# Revit family: FY-B-TY3451_Imperial
name_source: partatom
category: Sprinklers
units: mm (PartAtom-declared; Revit-internal decimal feet)

## family parameters
Always vertical = Yes
Cut with Voids When Loaded = No
Maintain Annotation Orientation = No
OmniClass Number = 23.65.70.17.11.24
OmniClass Title = Fire Fighting Sprinkler Heads
Part Type = Normal
Room Calculation Point = No
Round Connector Dimension = Use Diameter
Shared = No
Work Plane-Based = No

## types (42) — shared parameters
COBie = Yes
COBie.Component.Name = Sprinklers:Vertical SW_SIN
COBie.Type = Yes
COBie.Type.AssetType = Fixed
COBie.Type.Category = Pr_70_55_97_84:Sprinklers
COBie.Type.Manufacturer = Tyco Fire Protection Products
COBie.Type.Material = Bronze
COBie.Type.NominalHeight = 0' - 0"
COBie.Type.NominalLength = 0' - 0"
COBie.Type.NominalWidth = 0' - 0"
COBie.Type.Shape = Cylinder
COBie.Type.WarrantyGuarantorParts = http://tycofsbp.com
TFPPTerms_of_Sale.pdf
Coverage = Standard
Coverage_ = Standard
Default Elevation = 0' - 0"
K-Factor = 5.5493
Manufacturer = Tyco Fire Protection Products
Manufacturer URL = www.tyco-fire.com
Material_ = Bronze
Model = TY-B
Nominal Diameter 1 = 1"
Orifice = Standard
Orifice Size = 0"
Outside Diameter 1 = 1"
Response = Standard
Response_ = Standard
SIN No = TY3451
Takeout 1 = 2"
Technical Data Sheet No = TFP161
zero-valued in all types: COBie.Type.ReplacementCost, Style Id

## per-type parameters (varying)
| type | COBie.Component.Description | COBie.Type.Colour | COBie.Type.DurationUnit | COBie.Type.Finish | COBie.Type.ModelNumber | COBie.Type.ModelReference | COBie.Type.Size | COBie.Type.WarrantyDescription | Description | Finish_ | Part No | Temperature Rating |
| Vertical Sidewall Brass 135°F/57°C 5.6K ½" NPT_57-575-1-135 | TY-B Wet Vertical SW  57.2°C K80 DN15 NPT Br | Yellow | year | Natural Brass | 57-575-1-135 | TY-B Wet Vertical SW  57.2°C K80 DN15 NPT Br | 1/2"(DN15) |  | TY-B Vertical Sidewall Brass 135°F/57°C 5.6K ½" NPT_57-575-1-135 | Natural Brass | 57-575-1-135 | 135 °F |
| Vertical Sidewall Brass 155°F/68°C 5.6K ½" NPT_57-575-1-155 | TY-B Wet Vertical SW  68.3°C K80 DN15 NPT Br | Yellow | year | Natural Brass | 57-575-1-155 | TY-B Wet Vertical SW  68.3°C K80 DN15 NPT Br | 1/2"(DN15) |  | TY-B Vertical Sidewall Brass 155°F/68°C 5.6K ½" NPT_57-575-1-155 | Natural Brass | 57-575-1-155 | 155 °F |
| Vertical Sidewall Brass 175°F/79°C 5.6K ½" NPT_57-575-1-175 | TY-B Wet Vertical SW  79.4°C K80 DN15 NPT Br | Yellow | year | natural Brass | 57-575-1-175 | TY-B Wet Vertical SW  79.4°C K80 DN15 NPT Br | 1/2"(DN15) |  | TY-B Vertical Sidewall Brass 175°F/79°C 5.6K ½" NPT_57-575-1-175 | Natural Brass | 57-575-1-175 | 175 °F |
| Vertical Sidewall Brass 200°F/93°C 5.6K ½" NPT_57-575-1-200 | TY-B Wet Vertical SW  93.3°C K80 DN15 NPT Br | Yellow | year | Natural Brass | 57-575-1-200 | TY-B Wet Vertical SW  93.3°C K80 DN15 NPT Br | 1/2"(DN15) |  | TY-B Vertical Sidewall Brass 200°F/93°C 5.6K ½" NPT_57-575-1-200 | Natural Brass | 57-575-1-200 | 200 °F |
| Vertical Sidewall Brass 286°F/141°C 5.6K ½" NPT_57-575-1-286 | TY-B Wet Vertical SW  141.1°C K80 DN15 NPT Br | Yellow | year | Natural Brass | 57-575-1-286 | TY-B Wet Vertical SW  141.1°C K80 DN15 NPT Br | 1/2"(DN15) |  | TY-B Vertical Sidewall Brass 286°F/141°C 5.6K ½" NPT_57-575-1-286 | Natural Brass | 57-575-1-286 | 286 °F |
| Vertical Sidewall Brass 360°F/182°C 5.6K ½" NPT_57-575-1-360 | TY-B Wet Vertical SW  182.2°C K80 DN15 NPT Br | Yellow | year | Natural Brass | 57-575-1-360 | TY-B Wet Vertical SW  182.2°C K80 DN15 NPT Br | 1/2"(DN15) |  | TY-B Vertical Sidewall Brass 360°F/182°C 5.6K ½" NPT_57-575-1-360 | Natural Brass | 57-575-1-360 | 360 °F |
| Vertical Sidewall White RAL9010 135°F/57°C 5.6K ½" NPT_57-575-3-135 | TY-B Wet Vertical SW  57.2°C K80 DN15 NPT Wh9010 | White | year | Pure White | 57-575-3-135 | TY-B Wet Vertical SW  57.2°C K80 DN15 NPT Wh9010 | 1/2"(DN15) |  | TY-B Vertical Sidewall White RAL9010 135°F/57°C 5.6K ½" NPT_57-575-3-135 | White RAL9010 | 57-575-3-135 | 135 °F |
| Vertical Sidewall White RAL9010 155°F/68°C 5.6K ½" NPT_57-575-3-155 | TY-B Wet Vertical SW  68.3°C K80 DN15 NPT Wh9010 | White |  | Pure White | 57-575-3-155 | TY-B Wet Vertical SW  68.3°C K80 DN15 NPT Wh9010 | 1/2"(DN15) |  | TY-B Vertical Sidewall White RAL9010 155°F/68°C 5.6K ½" NPT_57-575-3-155 | White RAL9010 | 57-575-3-155 | 155 °F |
| Vertical Sidewall White RAL9010 175°F/79°C 5.6K ½" NPT_57-575-3-175 | TY-B Wet Vertical SW  79.4°C K80 DN15 NPT Wh9010 | White | year | Pure White | 57-575-3-175 | TY-B Wet Vertical SW  79.4°C K80 DN15 NPT Wh9010 | 1/2"'(DN15) |  | TY-B Vertical Sidewall White RAL9010 175°F/79°C 5.6K ½" NPT_57-575-3-175 | White RAL9010 | 57-575-3-175 | 175 °F |
| Vertical Sidewall White RAL9010 200°F/93°C 5.6K ½" NPT_57-575-3-200 | TY-B Wet Vertical SW  93.3°C K80 DN15 NPT Wh9010 | White | year | Pure White | 57-575-3-200 | TY-B Wet Vertical SW  93.3°C K80 DN15 NPT Wh9010 | 1/2"(DN15) |  | TY-B Vertical Sidewall White RAL9010 200°F/93°C 5.6K ½" NPT_57-575-3-200 | White RAL9010 | 57-575-3-200 | 200 °F |
| Vertical Sidewall White RAL9010 286°F/141°C 5.6K ½" NPT_57-575-3-286 | TY-B Wet Vertical SW  141.1°C K80 DN15 NPT Wh9010 | White | year | Pure White | 57-575-3-286 | TY-B Wet Vertical SW  141.1°C K80 DN15 NPT Wh9010 | 1/2"(DN15) |  | TY-B Vertical Sidewall White RAL9010 286°F/141°C 5.6K ½" NPT_57-575-3-286 | White RAL9010 | 57-575-3-286 | 286 °F |
| Vertical Sidewall White RAL9010 360°F/182°C 5.6K ½" NPT_57-575-3-360 | TY-B Wet Vertical SW  182.2°C K80 DN15 NPT Wh9010 | White | year | Pure White | 57-575-3-360 | TY-B Wet Vertical SW  182.2°C K80 DN15 NPT Wh9010 | 1/2"(DN15) |  | TY-B Vertical Sidewall White RAL9010 360°F/182°C 5.6K ½" NPT_57-575-3-360 | White RAL9010 | 57-575-3-360 | 360 °F |
| Vertical Sidewall White 135°F/57°C 5.6K ½" NPT_57-575-4-135 | TY-B Wet Vertical SW  57.2°C K80 DN15 NPT Wh9003 | White | year | Signal White | 57-575-4-135 | TY-B Wet Vertical SW  57.2°C K80 DN15 NPT Wh9003 | 1/2"(DN15) |  | TY-B Vertical Sidewall White 135°F/57°C 5.6K ½" NPT_57-575-4-135 | White RAL9003 | 57-575-4-135 | 135 °F |
| Vertical Sidewall White 155°F/68°C 5.6K ½" NPT_57-575-4-155 | TY-B Wet Vertical SW  68.3°C K80 DN15 NPT Wh9003 | White | year | Signal White | 57-575-4-155 | TY-B Wet Vertical SW  68.3°C K80 DN15 NPT Wh9003 | 1/2"(DN15) |  | TY-B Vertical Sidewall White 155°F/68°C 5.6K ½" NPT_57-575-4-155 | White RAL9003 | 57-575-4-155 | 155 °F |
| Vertical Sidewall White 175°F/79°C 5.6K ½" NPT_57-575-4-175 | TY-B Wet Vertical SW  79.4°C K80 DN15 NPT Wh9003 | White | year | Signal White | 57-575-4-175 | TY-B Wet Vertical SW  79.4°C K80 DN15 NPT Wh9003 | 1/2"(DN15) |  | TY-B Vertical Sidewall White 175°F/79°C 5.6K ½" NPT_57-575-4-175 | White RAL9003 | 57-575-4-175 | 175 °F |
| Vertical Sidewall White 200°F/93°C 5.6K ½" NPT_57-575-4-200 | TY-B Wet Vertical SW  93.3°C K80 DN15 NPT Wh9003 | White | year | Signal White | 57-575-4-200 | TY-B Wet Vertical SW  93.3°C K80 DN15 NPT Wh9003 | 1/2"(DN15) |  | TY-B Vertical Sidewall White 200°F/93°C 5.6K ½" NPT_57-575-4-200 | White RAL9003 | 57-575-4-200 | 200 °F |
| Vertical Sidewall White 286°F/141°C 5.6K ½" NPT_57-575-4-286 | TY-B Wet Vertical SW  141.1°C K80 DN15 NPT Wh9003 | White | year | Signal White | 57-575-4-286 | TY-B Wet Vertical SW  141.1°C K80 DN15 NPT Wh9003 | 1/2"(DN15) | On-site Sprinkler Replacement Warranty | TY-B Vertical Sidewall White 286°F/141°C 5.6K ½" NPT_57-575-4-286 | White RAL9003 | 57-575-4-286 | 286 °F |
| Vertical Sidewall White 360°F/182°C 5.6K ½" NPT_57-575-4-360 | TY-B Wet Vertical SW  182.2°C K80 DN15 NPT Wh9003 | White | year | Signal White | 57-575-4-360 | TY-B Wet Vertical SW  182.2°C K80 DN15 NPT Wh9003 | 1/2"(DN15) |  | TY-B Vertical Sidewall White 360°F/182°C 5.6K ½" NPT_57-575-4-360 | White RAL9003 | 57-575-4-360 | 360 °F |
| Vertical Sidewall JetBlack 155°F/68°C 5.6K ½" NPT_57-575-5-155 | TY-B Wet Vertical SW  68.3°C K80 DN15 NPT JBlk | Black | year | Jet Black | 57-575-5-155 | TY-B Wet Vertical SW  68.3°C K80 DN15 NPT JBlk | 1/2"(DN15) |  | TY-B Vertical Sidewall JetBlack 155°F/68°C 5.6K ½" NPT_57-575-5-155 | Jet Black RAL9005 | 57-575-5-155 | 155 °F |
| Vertical Sidewall JetBlack 200°F/93°C 5.6K ½" NPT_57-575-5-200 | TY-B Wet Vertical SW  93.3°C K80 DN15 NPT JBlk | Black | year | Jet Black | 57-575-5-200 | TY-B Wet Vertical SW  93.3°C K80 DN15 NPT JBlk | 1/2"(DN15) |  | TY-B Vertical Sidewall JetBlack 200°F/93°C 5.6K ½" NPT_57-575-5-200 | Jet Black RAL9005 | 57-575-5-200 | 200 °F |
| Vertical Sidewall Wax 135°F/57°C 5.6K ½" NPT_57-575-6-135 | TY-B Wet Vertical SW  57.2°C K80 DN15 NPT Wx | Gray | year | Wax Coated | 57-575-6-135 | TY-B Wet Vertical SW  57.2°C K80 DN15 NPT Wx | 1/2"(DN15) |  | TY-B Vertical Sidewall Wax 135°F/57°C 5.6K ½" NPT_57-575-6-135 | Wax Coated | 57-575-6-135 | 135 °F |
| Vertical Sidewall Wax 155°F/68°C 5.6K ½" NPT_57-575-6-155 | TY-B Wet Vertical SW  68.3°C K80 DN15 NPT Wx | Gray | year | Wax Coated | 57-575-6-155 | TY-B Wet Vertical SW  68.3°C K80 DN15 NPT Wx | 1/2"(DN15) |  | TY-B Vertical Sidewall Wax 155°F/68°C 5.6K ½" NPT_57-575-6-155 | Wax Coated | 57-575-6-155 | 155 °F |
| Vertical Sidewall Wax 175°F/79°C 5.6K ½" NPT_57-575-6-175 | TY-B Wet Vertical SW  79.4°C K80 DN15 NPT Wx | Gray | year | Wax Coated | 57-575-6-175 | TY-B Wet Vertical SW  79.4°C K80 DN15 NPT Wx | 1/2"(DN15) |  | TY-B Vertical Sidewall Wax 175°F/79°C 5.6K ½" NPT_57-575-6-175 | Wax Coated | 57-575-6-175 | 175 °F |
| Vertical Sidewall Wax 200°F/93°C 5.6K ½" NPT_57-575-6-200 | TY-B Wet Vertical SW  93.3°C K80 DN15 NPT Wx | Gray | year | Wax Coated | 57-575-6-200 | TY-B Wet Vertical SW  93.3°C K80 DN15 NPT Wx | 1/2"(DN15) |  | TY-B Vertical Sidewall Wax 200°F/93°C 5.6K ½" NPT_57-575-6-200 | Wax Coated | 57-575-6-200 | 200 °F |
| Vertical Sidewall Wax 286°F/141°C 5.6K ½" NPT_57-575-6-286 | TY-B Wet Vertical SW  141.1°C K80 DN15 NPT Wx | Gray | year | Wax Coated | 57-575-6-286 | TY-B Wet Vertical SW  141.1°C K80 DN15 NPT Wx | 1/2"(DN15) |  | TY-B Vertical Sidewall Wax 286°F/141°C 5.6K ½" NPT_57-575-6-286 | Wax Coated | 57-575-6-286 | 286 °F |
| Vertical Sidewall Lead 135°F/57°C 5.6K ½" NPT_57-575-7-135 | TY-B Wet Vertical SW  57.2°C K80 DN15 NPT Lead | Gray | year | Lead Coated | 57-575-7-135 | TY-B Wet Vertical SW  57.2°C K80 DN15 NPT Lead | 1/2"(DN15) |  | TY-B Vertical Sidewall Lead 135°F/57°C 5.6K ½" NPT_57-575-7-135 | Lead Coated | 57-575-7-135 | 135 °F |
| Vertical Sidewall Lead 155°F/68°C 5.6K ½" NPT_57-575-7-155 | TY-B Wet Vertical SW  68.3°C K80 DN15 NPT Lead | Gray | year | Lead Coated | 57-575-7-155 | TY-B Wet Vertical SW  68.3°C K80 DN15 NPT Lead | 1/2"(DN15) |  | TY-B Vertical Sidewall Lead 155°F/68°C 5.6K ½" NPT_57-575-7-155 | Lead Coated | 57-575-7-155 | 155 °F |
| Vertical Sidewall Lead 175°F/79°C 5.6K ½" NPT_57-575-7-175 | TY-B Wet Vertical SW  79.4°C K80 DN15 NPT Lead | Gray | year | Lead Coated | 57-575-7-175 | TY-B Wet Vertical SW  79.4°C K80 DN15 NPT Lead | 1/2"(DN15) |  | TY-B Vertical Sidewall Lead 175°F/79°C 5.6K ½" NPT_57-575-7-175 | Lead Coated | 57-575-7-175 | 175 °F |
| Vertical Sidewall Lead 200°F/93°C 5.6K ½" NPT_57-575-7-200 | TY-B Wet Vertical SW  93.3°C K80 DN15 NPT Lead | Gray | year | Lead Coated | 57-575-7-200 | TY-B Wet Vertical SW  93.3°C K80 DN15 NPT Lead | 1/2"(DN15) |  | TY-B Vertical Sidewall Lead 200°F/93°C 5.6K ½" NPT_57-575-7-200 | Lead Coated | 57-575-7-200 | 200 °F |
| Vertical Sidewall Lead 286°F/141°C 5.6K ½" NPT_57-575-7-286 | TY-B Wet Vertical SW  141.1°C K80 DN15 NPT Lead | Gray | year | Lead Coated | 57-575-7-286 | TY-B Wet Vertical SW  141.1°C K80 DN15 NPT Lead | 1/2"(DN15) |  | TY-B Vertical Sidewall Lead 286°F/141°C 5.6K ½" NPT_57-575-7-286 | Lead Coated | 57-575-7-286 | 286 °F |
| Vertical Sidewall Lead 360°F/182°C 5.6K ½" NPT_57-575-7-360 | TY-B Wet Vertical SW  182.2°C K80 DN15 NPT Lead | Gray | year | Lead Coated | 57-575-7-360 | TY-B Wet Vertical SW  182.2°C K80 DN15 NPT Lead | 1/2"(DN15) |  | TY-B Vertical Sidewall Lead 360°F/182°C 5.6K ½" NPT_57-575-7-360 | Lead Coated | 57-575-7-360 | 360 °F |
| Vertical Sidewall Wax Over Lead 135°F/57°C 5.6K ½" NPT_57-575-8-135 | TY-B Wet Vertical SW  57.2°C K80 DN15 NPT WoL | Gray | year | Wax Over Lead | 57-575-8-135 | TY-B Wet Vertical SW  57.2°C K80 DN15 NPT WoL | 1/2"(DN15) |  | TY-B Vertical Sidewall Wax Over Lead 135°F/57°C 5.6K ½" NPT_57-575-8-135 | Wax Over Lead | 57-575-8-135 | 135 °F |
| Vertical Sidewall Wax Over Lead 155°F/68°C 5.6K ½" NPT_57-575-8-155 | TY-B Wet Vertical SW  68.3°C K80 DN15 NPT WoL | Gray | year | Wax Over Lead | 57-575-8-155 | TY-B Wet Vertical SW  68.3°C K80 DN15 NPT WoL | 1/2"(DN15) |  | TY-B Vertical Sidewall Wax Over Lead 155°F/68°C 5.6K ½" NPT_57-575-8-155 | Wax Over Lead | 57-575-8-155 | 155 °F |
| Vertical Sidewall Wax Over Lead 175°F/79°C 5.6K ½" NPT_57-575-8-175 | TY-B Wet Vertical SW  79.4°C K80 DN15 NPT WoL | Gray | year | Wax Over Lead | 57-575-8-175 | TY-B Wet Vertical SW  79.4°C K80 DN15 NPT WoL | 1/2"(DN15) |  | TY-B Vertical Sidewall Wax Over Lead 175°F/79°C 5.6K ½" NPT_57-575-8-175 | Wax Over Lead | 57-575-8-175 | 175 °F |
| Vertical Sidewall Wax Over Lead 200°F/93°C 5.6K ½" NPT_57-575-8-200 | TY-B Wet Vertical SW  93.3°C K80 DN15 NPT WoL | Gray | year | Wax Over Lead | 57-575-8-200 | TY-B Wet Vertical SW  93.3°C K80 DN15 NPT WoL | 1/2"(DN15) |  | TY-B Vertical Sidewall Wax Over Lead 200°F/93°C 5.6K ½" NPT_57-575-8-200 | Wax Over Lead | 57-575-8-200 | 200 °F |
| Vertical Sidewall Wax Over Lead 286°F/141°C 5.6K ½" NPT_57-575-8-286 | TY-B Wet Vertical SW  141.1°C K80 DN15 NPT WoL | Gray | year | Wax Over lead | 57-575-8-286 | TY-B Wet Vertical SW  141.1°C K80 DN15 NPT WoL | 1/2"(DN15) |  | TY-B Vertical Sidewall Wax Over Lead 286°F/141°C 5.6K ½" NPT_57-575-8-286 | Wax Over Lead | 57-575-8-286 | 286 °F |
| Vertical Sidewall Chrome 135°F/57°C 5.6K ½" NPT_57-575-9-135 | TY-B Wet Vertical SW  57.2°C K80 DN15 NPT Chr | Silver | year | Chrome Plated | 57-575-9-135 | TY-B Wet Vertical SW  57.2°C K80 DN15 NPT Chr | 1/2"(DN15) |  | TY-B Vertical Sidewall Chrome 135°F/57°C 5.6K ½" NPT_57-575-9-135 | Chrome Plated | 57-575-9-135 | 135 °F |
| Vertical Sidewall Chrome 155°F/68°C 5.6K ½" NPT_57-575-9-155 | TY-B Wet Vertical SW  68.3°C K80 DN15 NPT Chr | Silver | year | Chrome Plated | 57-575-9-155 | TY-B Wet Vertical SW  68.3°C K80 DN15 NPT Chr | 1/2"(DN15) |  | TY-B Vertical Sidewall Chrome 155°F/68°C 5.6K ½" NPT_57-575-9-155 | Chrome Plated | 57-575-9-155 | 155 °F |
| Vertical Sidewall Chrome 175°F/79°C 5.6K ½" NPT_57-575-9-175 | TY-B Wet Vertical SW  79.4°C K80 DN15 NPT Chr | Silver | year | Chrome Plated | 57-575-9-175 | TY-B Wet Vertical SW  79.4°C K80 DN15 NPT Chr | 1/2"(DN15) |  | TY-B Vertical Sidewall Chrome 175°F/79°C 5.6K ½" NPT_57-575-9-175 | Chrome Plated | 57-575-9-175 | 175 °F |
| Vertical Sidewall Chrome 200°F/93°C 5.6K ½" NPT_57-575-9-200 | TY-B Wet Vertical SW  93.3°C K80 DN15 NPT Chr | Silver | year | Chrome Plated | 57-575-9-200 | TY-B Wet Vertical SW  93.3°C K80 DN15 NPT Chr | 1/2"(DN15) |  | TY-B Vertical Sidewall Chrome 200°F/93°C 5.6K ½" NPT_57-575-9-200 | Chrome Plated | 57-575-9-200 | 200 °F |
| Vertical Sidewall Chrome 286°F/141°C 5.6K ½" NPT_57-575-9-286 | TY-B Wet Vertical SW  141.1°C K80 DN15 NPT Chr | Silver | year | Chrome Plated | 57-575-9-286 | TY-B Wet Vertical SW  141.1°C K80 DN15 NPT Chr | 1/2"(DN15) |  | TY-B Vertical Sidewall Chrome 286°F/141°C 5.6K ½" NPT_57-575-9-286 | Chrome Plated | 57-575-9-286 | 286 °F |
| Vertical Sidewall Chrome 360°F/182°C 5.6K ½" NPT_57-575-9-360 | TY-B Wet Vertical SW  182.2°C K80 DN15 NPT Chr | Silver | year | Chrome Plated | 57-575-9-360 | TY-B Wet Vertical SW  182.2°C K80 DN15 NPT Chr | 1/2"(DN15) |  | TY-B Vertical Sidewall Chrome 360°F/182°C 5.6K ½" NPT_57-575-9-360 | Chrome Plated | 57-575-9-360 | 360 °F |

## geometry (parser evidence)
native form markers: Blend x2, Sweep x54
no freeform markers — native parametric forms only
